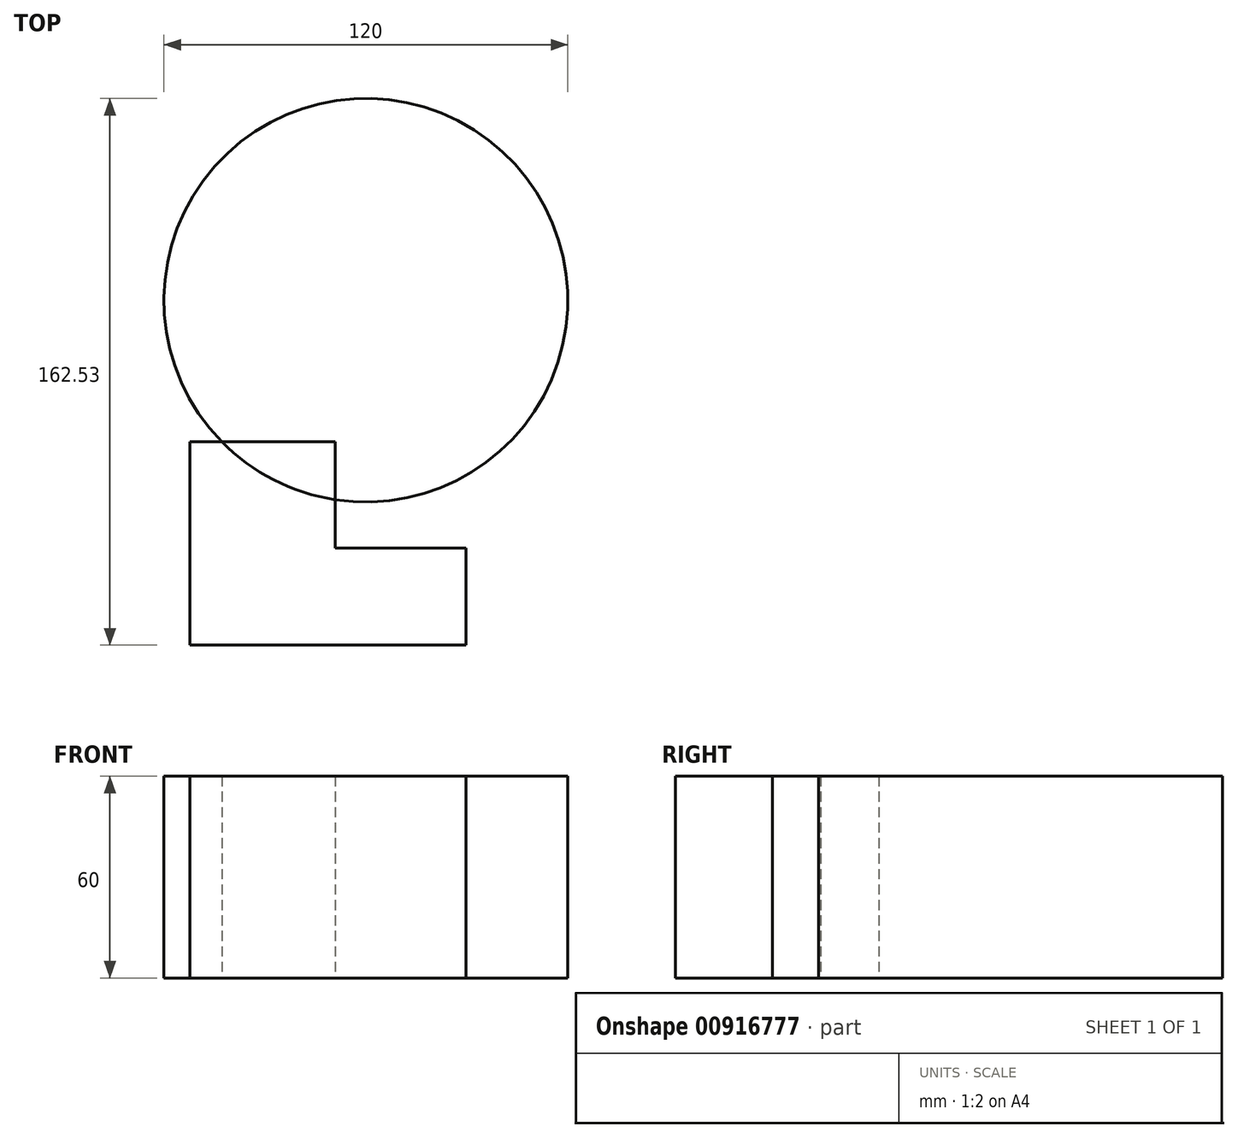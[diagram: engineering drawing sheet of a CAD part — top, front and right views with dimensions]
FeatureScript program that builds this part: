
annotation { "Feature Type Name" : "Feature", "Feature Type Description" : "" }
export const myFeature = defineFeature(function(context is Context, id is Id, definition is map)
    precondition{}
    {
        {
            var Q0;
            Q0=qCreatedBy(makeId("Top.planeOp"),FACE);
            var sketch = newSketch(context, id + "F0", { "sketchPlane" : qUnion([Q0])});
            skLineSegment(sketch, "E0", {"start": v(0, 0) * mm, "end": v(0, 60.49) * mm});
            skLineSegment(sketch, "E1", {"start": v(0, 60.49) * mm, "end": v(43.12, 60.49) * mm});
            skLineSegment(sketch, "E2", {"start": v(43.12, 60.49) * mm, "end": v(43.12, 28.78) * mm});
            skLineSegment(sketch, "E3", {"start": v(43.12, 28.78) * mm, "end": v(82.05, 28.78) * mm});
            skLineSegment(sketch, "E4", {"start": v(82.05, 28.78) * mm, "end": v(82.05, 0) * mm});
            skLineSegment(sketch, "E5", {"start": v(0, 0) * mm, "end": v(82.05, 0) * mm});
            skSolve(sketch);
        }
        {
            var Q0;
            Q0=makeQuery(id+"F0.imprint","IMPRINT",FACE,{"disambiguationData":[TD([[makeQuery(id+"F0.imprint","IMPRINT",EDGE,{"derivedFrom":sQuery(id+"F0.wireOp",EDGE,"E0")}),-1.0]])]});
            var sketch = newSketch(context, id + "F1", { "sketchPlane" : qUnion([Q0])});
            skCircle(sketch, "E6", {"center": v(52.26, 102.53) * mm, "radius": 60 * mm});
            skLineSegment(sketch, "E7", {"start": v(52.26, 102.53) * mm, "end": v(52.26, 162.53) * mm});
            skSolve(sketch);
        }
        {
            var Q0;
            {var subQ1=makeQuery(id+"F0.imprint","IMPRINT",EDGE,{"derivedFrom":sQuery(id+"F0.wireOp",EDGE,"E0")});Q0=makeQuery(id+"F1.imprint","IMPRINT",FACE,{"disambiguationData":[TD([[makeQuery(id+"F1.imprint","IMPRINT",EDGE,{"derivedFrom":subQ1}),-1.0]])]});}
            var Q1;
            {var subQ0=sQuery(id+"F1.wireOp",EDGE,"E6");var subQ1=makeQuery(id+"F1.imprint","IMPRINT",VERTEX,{"derivedFrom":subQ0});Q1=makeQuery(id+"F1.imprint","IMPRINT",FACE,{"disambiguationData":[TD([[makeQuery(id+"F1.imprint","IMPRINT",EDGE,{"disambiguationData":[TD([[subQ1,-1.0]])],"derivedFrom":subQ0}),1.0]])]});}
            extrude(context, id + "F2", {"entities" : qUnion([Q0, Q1]), "endBound" : BoundingType.SYMMETRIC, "depth" : 60 * mm, "offsetDistance" : 25 * mm});
        }
        {
            var Q0;
            Q0=makeQuery(id+"F2.opExtrude","CAP_FACE",FACE,{"disambiguationData":[OSD([sQuery(id+"F0.wireOp",EDGE,"E1"),sQuery(id+"F0.wireOp",EDGE,"E2"),sQuery(id+"F1.wireOp",EDGE,"E6")])],"isStart":false});
            var sketch = newSketch(context, id + "F3", { "sketchPlane" : qUnion([Q0])});
            skCircle(sketch, "E8", {"center": v(52.26, 102.53) * mm, "radius": 29.7 * mm});
            skSolve(sketch);
        }
        {
            var Q0;
            Q0=makeQuery(id+"F3.imprint","IMPRINT",FACE,{"disambiguationData":[TD([[makeQuery(id+"F3.imprint","IMPRINT",EDGE,{"derivedFrom":sQuery(id+"F3.wireOp",EDGE,"E8")}),-1.0]])]});
            cPlane(context, id + "F4", {"entities" : qUnion([Q0]), "cplaneType" : CPlaneType.OFFSET, "offset" : 50 * mm, "width" : 150 * mm, "height" : 150 * mm});
        }
    });
